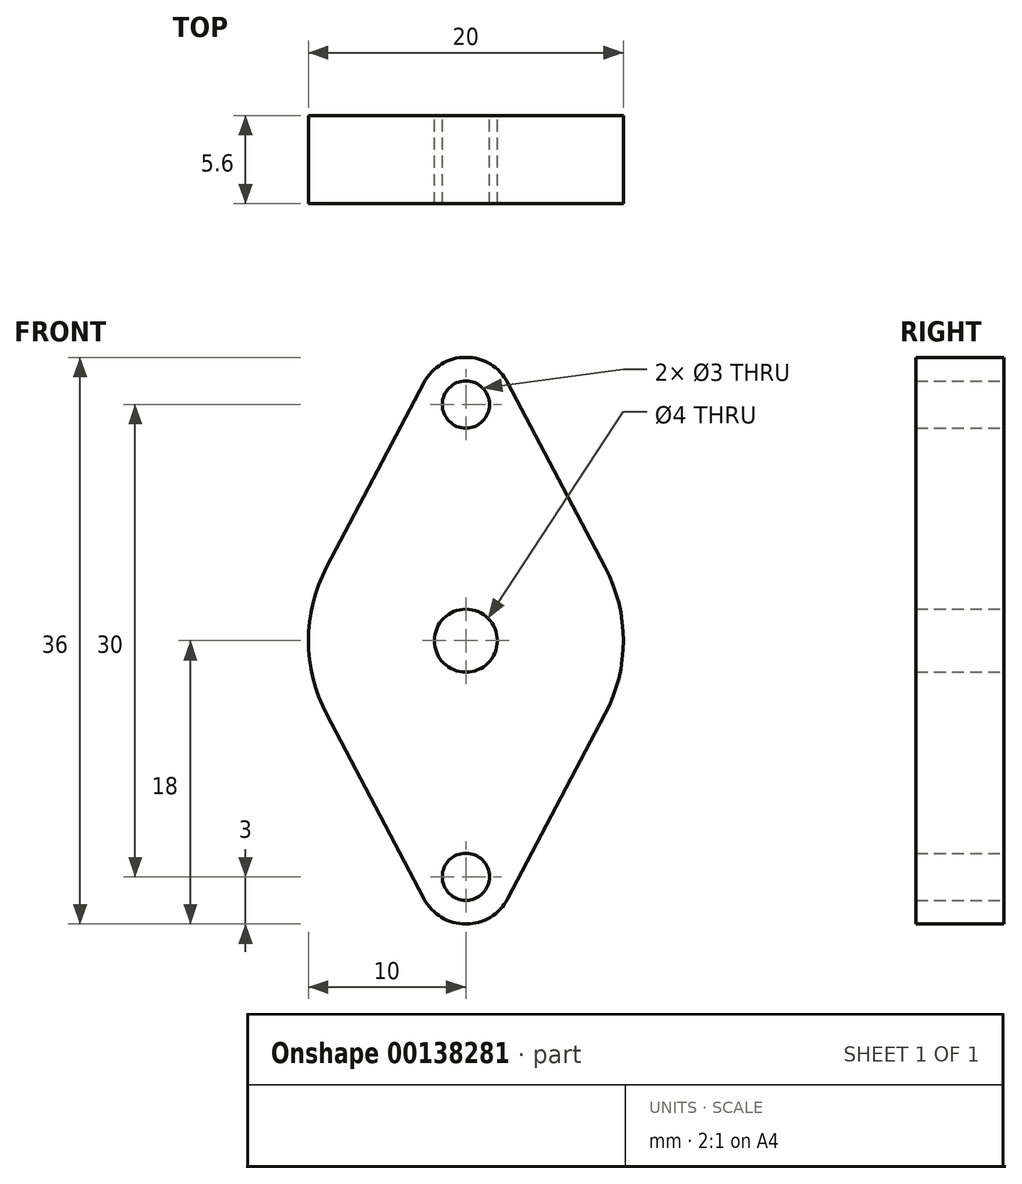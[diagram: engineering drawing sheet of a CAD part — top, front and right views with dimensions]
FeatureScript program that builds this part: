
annotation { "Feature Type Name" : "Feature", "Feature Type Description" : "" }
export const myFeature = defineFeature(function(context is Context, id is Id, definition is map)
    precondition{}
    {
        {
            var Q0;
            Q0=qCreatedBy(makeId("Front.planeOp"),FACE);
            var sketch = newSketch(context, id + "F0", { "sketchPlane" : qUnion([Q0])});
            skCircle(sketch, "E0", {"center": v(0, 0) * mm, "radius": 8 * mm, "construction": true});
            skCircle(sketch, "E1", {"center": v(0, 0) * mm, "radius": 2 * mm});
            skCircle(sketch, "E2", {"center": v(0, 0) * mm, "radius": 10 * mm, "construction": true});
            skCircle(sketch, "E3", {"center": v(0, 15) * mm, "radius": 1.5 * mm});
            skCircle(sketch, "E4", {"center": v(0, 15) * mm, "radius": 3 * mm, "construction": true});
            skLineSegment(sketch, "E5", {"start": v(-8.84, 4.67) * mm, "end": v(-2.65, 16.4) * mm});
            skLineSegment(sketch, "E6.MirrorCS", {"start": v(8.84, 4.67) * mm, "end": v(2.65, 16.4) * mm});
            skArc(sketch, "E7", {"start": v(2.65, 16.4) * mm, "mid": v(0, 18) * mm, "end": v(-2.65, 16.4) * mm});
            skLineSegment(sketch, "E8.MirrorCS", {"start": v(-8.84, -4.67) * mm, "end": v(-2.65, -16.4) * mm});
            skArc(sketch, "E9.MirrorCS", {"start": v(2.65, -16.4) * mm, "mid": v(0, -18) * mm, "end": v(-2.65, -16.4) * mm});
            skLineSegment(sketch, "E10.MirrorCS", {"start": v(8.84, -4.67) * mm, "end": v(2.65, -16.4) * mm});
            skArc(sketch, "E11", {"start": v(-8.84, 4.67) * mm, "mid": v(-10, 0) * mm, "end": v(-8.84, -4.67) * mm});
            skArc(sketch, "E12", {"start": v(8.84, -4.67) * mm, "mid": v(10, 0) * mm, "end": v(8.84, 4.67) * mm});
            skCircle(sketch, "E13.MirrorC", {"center": v(0, -15) * mm, "radius": 1.5 * mm});
            skSolve(sketch);
        }
        {
            var Q0;
            Q0=makeQuery(id+"F0.imprint","IMPRINT",FACE,{"disambiguationData":[TD([[makeQuery(id+"F0.imprint","IMPRINT",EDGE,{"derivedFrom":sQuery(id+"F0.wireOp",EDGE,"E1")}),-1.0]])]});
            extrude(context, id + "F1", {"entities" : qUnion([Q0]), "depth" : 5.6 * mm});
        }
    });
